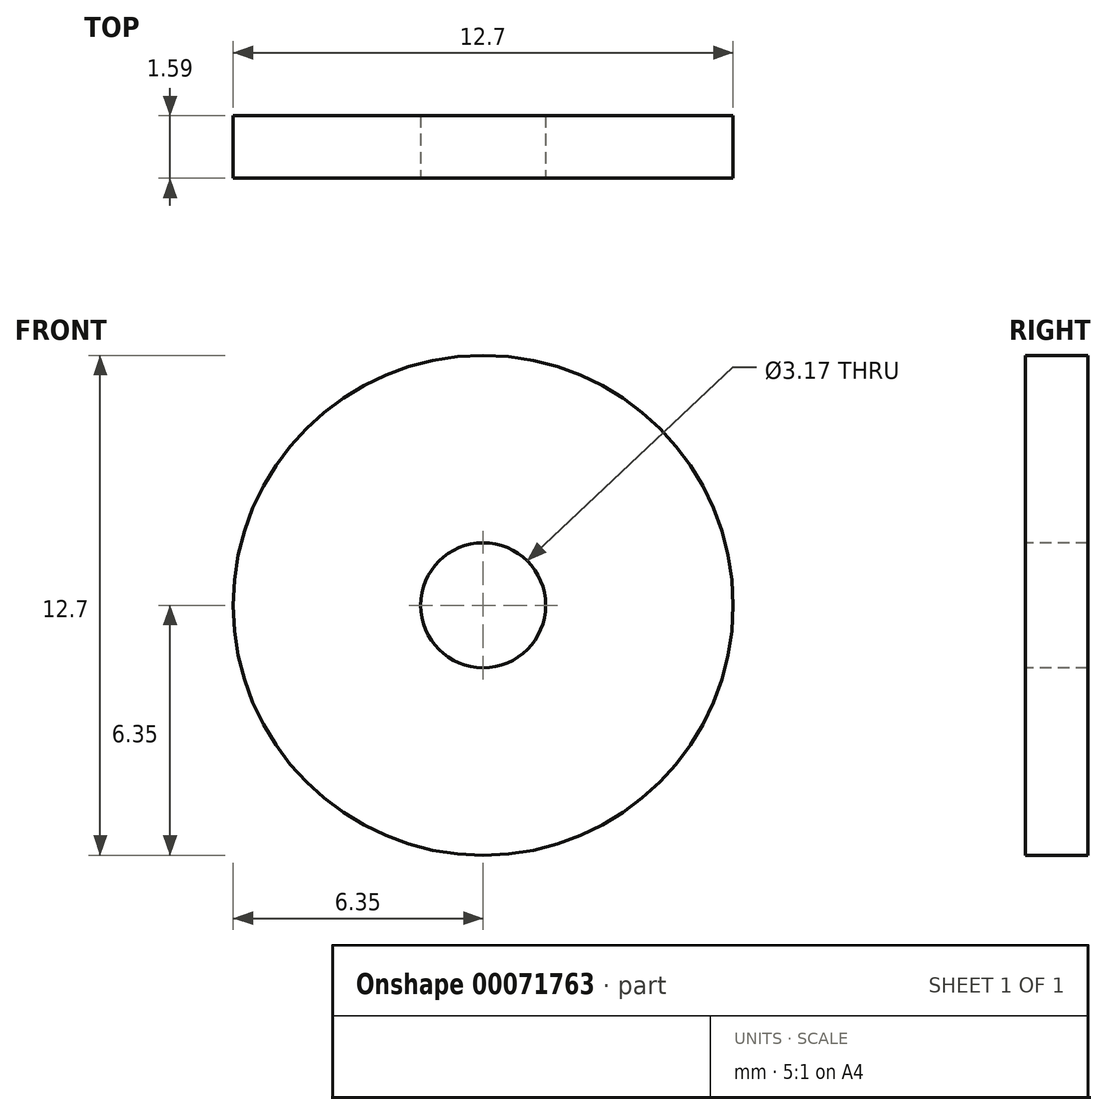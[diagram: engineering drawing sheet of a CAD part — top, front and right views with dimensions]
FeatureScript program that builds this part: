
annotation { "Feature Type Name" : "Feature", "Feature Type Description" : "" }
export const myFeature = defineFeature(function(context is Context, id is Id, definition is map)
    precondition{}
    {
        {
            var Q0;
            Q0=qCreatedBy(makeId("Front.planeOp"),FACE);
            var sketch = newSketch(context, id + "F0", { "sketchPlane" : qUnion([Q0])});
            skCircle(sketch, "E0", {"center": v(0, 0) * mm, "radius": 6.35 * mm});
            skSolve(sketch);
        }
        {
            var Q0;
            Q0=qSketchRegion(id+"F0",true);
            extrude(context, id + "F1", {"entities" : qUnion([Q0]), "depth" : 1.59 * mm});
        }
        {
            var Q0;
            Q0=makeQuery(id+"F1.opExtrude","CAP_FACE",FACE,{"disambiguationData":[OSD([sQuery(id+"F0.wireOp",EDGE,"E0")])],"isStart":false});
            var sketch = newSketch(context, id + "F2", { "sketchPlane" : qUnion([Q0])});
            skCircle(sketch, "E1.0", {"center": v(0, 0) * mm, "radius": 6.35 * mm});
            skCircle(sketch, "E2", {"center": v(0, 0) * mm, "radius": 1.59 * mm});
            skSolve(sketch);
        }
        {
            var Q0;
            Q0=makeQuery(id+"F2.imprint","IMPRINT",FACE,{"disambiguationData":[TD([[makeQuery(id+"F2.imprint","IMPRINT",EDGE,{"derivedFrom":sQuery(id+"F2.wireOp",EDGE,"E2")}),1.0]])]});
            extrude(context, id + "F3", {"entities" : qUnion([Q0]), "operationType" : NewBodyOperationType.REMOVE, "endBound" : BoundingType.THROUGH_ALL, "oppositeDirection" : true, "depth" : 25.4 * mm});
        }
    });
